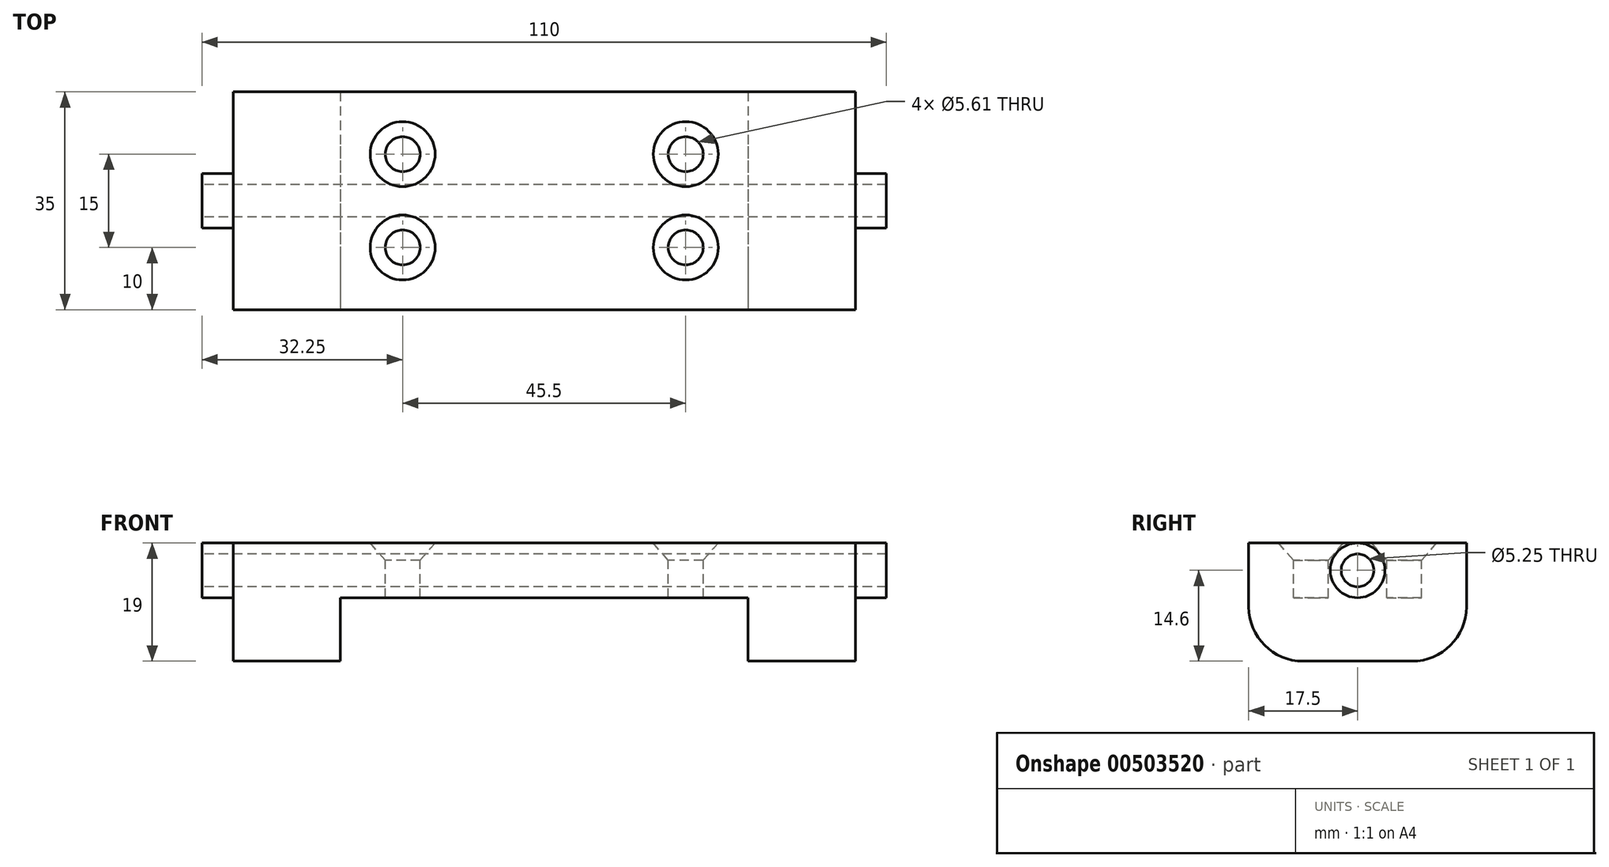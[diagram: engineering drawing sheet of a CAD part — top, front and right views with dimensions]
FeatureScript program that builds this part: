
annotation { "Feature Type Name" : "Feature", "Feature Type Description" : "" }
export const myFeature = defineFeature(function(context is Context, id is Id, definition is map)
    precondition{}
    {
        {
            var Q0;
            Q0=qCreatedBy(makeId("Top.planeOp"),FACE);
            var sketch = newSketch(context, id + "F0", { "sketchPlane" : qUnion([Q0])});
            skLineSegment(sketch, "E0.bottom", {"start": v(32.75, 17.5) * mm, "end": v(-32.75, 17.5) * mm});
            skLineSegment(sketch, "E0.top", {"start": v(32.75, -17.5) * mm, "end": v(-32.75, -17.5) * mm});
            skLineSegment(sketch, "E0.left", {"start": v(32.75, 17.5) * mm, "end": v(32.75, -17.5) * mm});
            skLineSegment(sketch, "E0.right", {"start": v(-32.75, 17.5) * mm, "end": v(-32.75, -17.5) * mm});
            skPoint(sketch, "E0.middle", {"position": v(0, 0) * mm});
            skLineSegment(sketch, "E1.bottom", {"start": v(-32.75, 17.5) * mm, "end": v(-50, 17.5) * mm});
            skLineSegment(sketch, "E1.top", {"start": v(-32.75, -17.5) * mm, "end": v(-50, -17.5) * mm});
            skLineSegment(sketch, "E1.right", {"start": v(-50, 17.5) * mm, "end": v(-50, -17.5) * mm});
            skLineSegment(sketch, "E2.bottom", {"start": v(32.75, 17.5) * mm, "end": v(50, 17.5) * mm});
            skLineSegment(sketch, "E2.top", {"start": v(32.75, -17.5) * mm, "end": v(50, -17.5) * mm});
            skLineSegment(sketch, "E2.right", {"start": v(50, 17.5) * mm, "end": v(50, -17.5) * mm});
            skSolve(sketch);
        }
        {
            var Q0;
            Q0=makeQuery(id+"F0.imprint","IMPRINT",FACE,{"disambiguationData":[TD([[makeQuery(id+"F0.imprint","IMPRINT",EDGE,{"derivedFrom":sQuery(id+"F0.wireOp",EDGE,"E0.bottom")}),1.0]])]});
            var Q1;
            Q1=makeQuery(id+"F0.imprint","IMPRINT",FACE,{"disambiguationData":[TD([[makeQuery(id+"F0.imprint","IMPRINT",EDGE,{"derivedFrom":sQuery(id+"F0.wireOp",EDGE,"E1.bottom")}),1.0]])]});
            var Q2;
            Q2=makeQuery(id+"F0.imprint","IMPRINT",FACE,{"disambiguationData":[TD([[makeQuery(id+"F0.imprint","IMPRINT",EDGE,{"derivedFrom":sQuery(id+"F0.wireOp",EDGE,"E2.bottom")}),-1.0]])]});
            extrude(context, id + "F1", {"entities" : qUnion([Q0, Q1, Q2]), "depth" : 1.5 * mm});
        }
        {
            var Q0;
            Q0=makeQuery(id+"F0.imprint","IMPRINT",FACE,{"disambiguationData":[TD([[makeQuery(id+"F0.imprint","IMPRINT",EDGE,{"derivedFrom":sQuery(id+"F0.wireOp",EDGE,"E1.bottom")}),1.0]])]});
            var Q1;
            Q1=makeQuery(id+"F0.imprint","IMPRINT",FACE,{"disambiguationData":[TD([[makeQuery(id+"F0.imprint","IMPRINT",EDGE,{"derivedFrom":sQuery(id+"F0.wireOp",EDGE,"E2.bottom")}),-1.0]])]});
            extrude(context, id + "F2", {"entities" : qUnion([Q0, Q1]), "operationType" : NewBodyOperationType.ADD, "oppositeDirection" : true, "depth" : (19 - 1.5) * mm});
        }
        {
            var Q0;
            Q0=makeQuery(id+"F0.imprint","IMPRINT",FACE,{"disambiguationData":[TD([[makeQuery(id+"F0.imprint","IMPRINT",EDGE,{"derivedFrom":sQuery(id+"F0.wireOp",EDGE,"E0.bottom")}),1.0]])]});
            extrude(context, id + "F3", {"entities" : qUnion([Q0]), "operationType" : NewBodyOperationType.ADD, "oppositeDirection" : true, "depth" : (8.8 - 1.5) * mm});
        }
        {
            var Q0;
            Q0=qCreatedBy(makeId("Right.planeOp"),FACE);
            var sketch = newSketch(context, id + "F4", { "sketchPlane" : qUnion([Q0])});
            skCircle(sketch, "E3", {"center": v(0, -2.9) * mm, "radius": 4.4 * mm});
            skCircle(sketch, "E4", {"center": v(0, -2.9) * mm, "radius": 2.62 * mm});
            skSolve(sketch);
        }
        {
            var Q0;
            Q0=makeQuery(id+"F4.imprint","IMPRINT",FACE,{"disambiguationData":[TD([[makeQuery(id+"F4.imprint","IMPRINT",EDGE,{"derivedFrom":sQuery(id+"F4.wireOp",EDGE,"E3")}),1.0]])]});
            var Q1;
            Q1=makeQuery(id+"F2.opExtrude","SWEPT_FACE",FACE,{"disambiguationData":[OSD([sQuery(id+"F0.wireOp",EDGE,"E0.left")])]});
            extrude(context, id + "F5", {"entities" : qUnion([Q0]), "operationType" : NewBodyOperationType.ADD, "offsetDistance" : 25 * mm, "depth" : 110 * mm, "symmetric" : true});
        }
        {
            var Q0;
            Q0=makeQuery(id+"F4.imprint","IMPRINT",FACE,{"disambiguationData":[TD([[makeQuery(id+"F4.imprint","IMPRINT",EDGE,{"derivedFrom":sQuery(id+"F4.wireOp",EDGE,"E4")}),1.0]])]});
            extrude(context, id + "F6", {"entities" : qUnion([Q0]), "operationType" : NewBodyOperationType.REMOVE, "endBound" : BoundingType.THROUGH_ALL, "oppositeDirection" : true, "depth" : 25 * mm, "hasSecondDirection" : true, "secondDirectionBound" : BoundingType.THROUGH_ALL, "secondDirectionOppositeDirection" : false, "secondDirectionDepth" : 25 * mm});
        }
        {
            var Q0;
            Q0=makeQuery(id+"F2.opExtrude","CAP_EDGE",EDGE,{"disambiguationData":[OSD([sQuery(id+"F0.wireOp",EDGE,"E2.top")])],"isStart":false});
            var Q1;
            Q1=makeQuery(id+"F2.opExtrude","CAP_EDGE",EDGE,{"disambiguationData":[OSD([sQuery(id+"F0.wireOp",EDGE,"E2.bottom")])],"isStart":false});
            var Q2;
            Q2=makeQuery(id+"F2.opExtrude","CAP_EDGE",EDGE,{"disambiguationData":[OSD([sQuery(id+"F0.wireOp",EDGE,"E1.top")])],"isStart":false});
            var Q3;
            Q3=makeQuery(id+"F2.opExtrude","CAP_EDGE",EDGE,{"disambiguationData":[OSD([sQuery(id+"F0.wireOp",EDGE,"E1.bottom")])],"isStart":false});
            fillet(context, id + "F7", {"entities" : qUnion([Q0, Q1, Q2, Q3]), "radius" : (19 - 1.5) / 2 * mm, "tangentPropagation" : true, "allowEdgeOverflow" : false});
        }
        {
            var Q0;
            Q0=makeQuery(id+"F1.opExtrude","CAP_FACE",FACE,{"disambiguationData":[OSD([sQuery(id+"F0.wireOp",EDGE,"E0.bottom"),sQuery(id+"F0.wireOp",EDGE,"E0.top"),sQuery(id+"F0.wireOp",EDGE,"E1.bottom"),sQuery(id+"F0.wireOp",EDGE,"E1.top"),sQuery(id+"F0.wireOp",EDGE,"E1.right"),sQuery(id+"F0.wireOp",EDGE,"E2.bottom"),sQuery(id+"F0.wireOp",EDGE,"E2.top"),sQuery(id+"F0.wireOp",EDGE,"E2.right")])],"isStart":false});
            var sketch = newSketch(context, id + "F8", { "sketchPlane" : qUnion([Q0])});
            skLineSegment(sketch, "E5.bottom", {"start": v(22.75, 7.5) * mm, "end": v(-22.75, 7.5) * mm});
            skLineSegment(sketch, "E5.top", {"start": v(22.75, -7.5) * mm, "end": v(-22.75, -7.5) * mm});
            skLineSegment(sketch, "E5.left", {"start": v(22.75, 7.5) * mm, "end": v(22.75, -7.5) * mm});
            skLineSegment(sketch, "E5.right", {"start": v(-22.75, 7.5) * mm, "end": v(-22.75, -7.5) * mm});
            skPoint(sketch, "E5.middle", {"position": v(0, 0) * mm});
            skSolve(sketch);
        }
        {
            var Q0;
            Q0=sQuery(id+"F8.wireOp",VERTEX,"E5.right.start");
            var Q1;
            Q1=sQuery(id+"F8.wireOp",VERTEX,"E5.right.end");
            var Q2;
            Q2=sQuery(id+"F8.wireOp",VERTEX,"E5.left.end");
            var Q3;
            Q3=sQuery(id+"F8.wireOp",VERTEX,"E5.left.start");
            var Q4;
            Q4=makeQuery(id+"F1.opExtrude","SWEPT_BODY",BODY,{"disambiguationData":[OSD([sQuery(id+"F0.wireOp",EDGE,"E0.bottom"),sQuery(id+"F0.wireOp",EDGE,"E0.top"),sQuery(id+"F0.wireOp",EDGE,"E1.bottom"),sQuery(id+"F0.wireOp",EDGE,"E1.top"),sQuery(id+"F0.wireOp",EDGE,"E1.right"),sQuery(id+"F0.wireOp",EDGE,"E2.bottom"),sQuery(id+"F0.wireOp",EDGE,"E2.top"),sQuery(id+"F0.wireOp",EDGE,"E2.right")])]});
            hole(context, id + "F9", {"style" : HoleStyle.C_SINK, "endStyle" : HoleEndStyle.THROUGH, "standardTappedOrClearance" : lookupTablePath({ "fit" : "Normal (ASME)", "standard" : "ANSI", "size" : "#10", "type" : "Clearance" }), "standardBlindInLast" : lookupTablePath({ "fit" : "Normal (ASME)", "standard" : "ANSI", "engagement" : "75%", "pitch" : "24 tpi", "size" : "#10", "type" : "Clearance & tapped" }), "holeDiameter" : 5.61 * mm, "cSinkDiameter" : 10.44 * mm, "cSinkAngle" : 82 * degree, "majorDiameter" : 5 * mm, "isTappedThrough" : true, "tappedDepth" : 46.25 * mm, "tapClearance" : 3, "locations" : qUnion([Q0, Q1, Q2, Q3]), "scope" : qUnion([Q4])});
        }
    });
